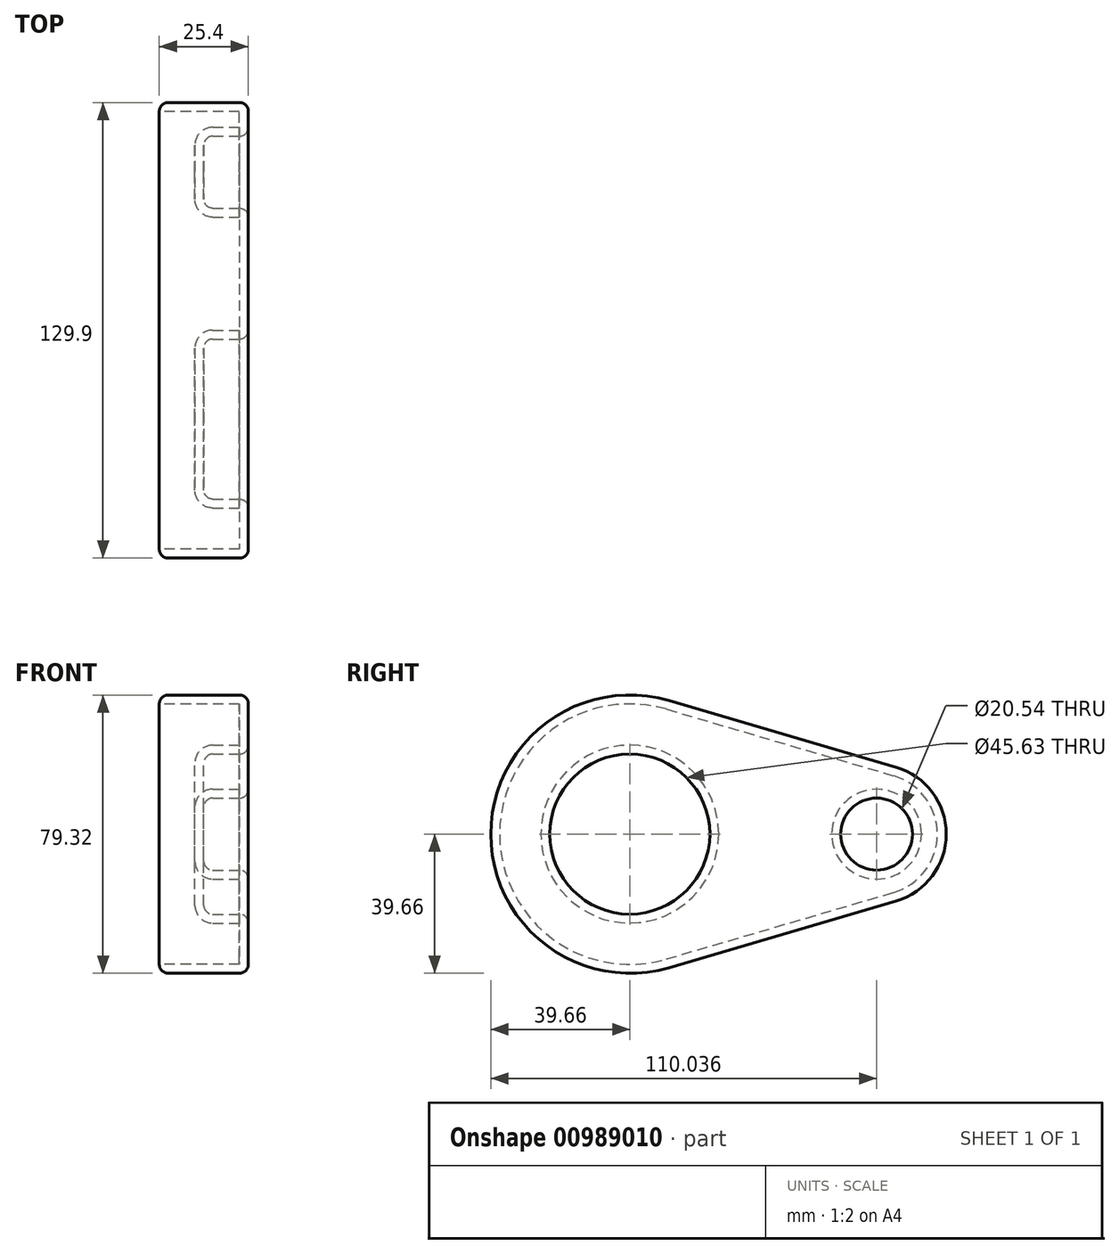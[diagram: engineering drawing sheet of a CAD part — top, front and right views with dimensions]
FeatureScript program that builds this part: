
annotation { "Feature Type Name" : "Feature", "Feature Type Description" : "" }
export const myFeature = defineFeature(function(context is Context, id is Id, definition is map)
    precondition{}
    {
        {
            var Q0;
            Q0=qCreatedBy(makeId("Right.planeOp"),FACE);
            var sketch = newSketch(context, id + "F0", { "sketchPlane" : qUnion([Q0])});
            skArc(sketch, "E0", {"start": v(11.15, 38.06) * mm, "mid": v(-39.66, 0) * mm, "end": v(11.15, -38.06) * mm});
            skArc(sketch, "E1", {"start": v(75.96, -19.06) * mm, "mid": v(90.24, 0) * mm, "end": v(75.96, 19.06) * mm});
            skLineSegment(sketch, "E2", {"start": v(11.15, 38.06) * mm, "end": v(75.96, 19.06) * mm});
            skLineSegment(sketch, "E3", {"start": v(11.15, -38.06) * mm, "end": v(75.96, -19.06) * mm});
            skSolve(sketch);
        }
        {
            var Q0;
            Q0=qSketchRegion(id+"F0",true);
            extrude(context, id + "F1", {"entities" : qUnion([Q0]), "depth" : 25.4 * mm});
        }
        {
            var Q0;
            Q0=makeQuery(id+"F1.opExtrude","CAP_FACE",FACE,{"disambiguationData":[OSD([sQuery(id+"F0.wireOp",EDGE,"E0"),sQuery(id+"F0.wireOp",EDGE,"E1"),sQuery(id+"F0.wireOp",EDGE,"E2"),sQuery(id+"F0.wireOp",EDGE,"E3")])],"isStart":false});
            var sketch = newSketch(context, id + "F2", { "sketchPlane" : qUnion([Q0])});
            skCircle(sketch, "E4", {"center": v(0, 0) * mm, "radius": 22.81 * mm});
            skCircle(sketch, "E5", {"center": v(70.38, 0) * mm, "radius": 10.27 * mm});
            skSolve(sketch);
        }
        {
            var Q0;
            Q0=qSketchRegion(id+"F2",true);
            extrude(context, id + "F3", {"entities" : qUnion([Q0]), "operationType" : NewBodyOperationType.REMOVE, "oppositeDirection" : true, "depth" : 12.7 * mm});
        }
        {
            var Q0;
            Q0=makeQuery(id+"F1.opExtrude","CAP_FACE",FACE,{"disambiguationData":[OSD([sQuery(id+"F0.wireOp",EDGE,"E0"),sQuery(id+"F0.wireOp",EDGE,"E1"),sQuery(id+"F0.wireOp",EDGE,"E2"),sQuery(id+"F0.wireOp",EDGE,"E3")])],"isStart":false});
            var Q1;
            Q1=makeQuery(id+"F3.boolean.opBoolean","COPY",FACE,{"derivedFrom":makeQuery(id+"F3.opExtrude","CAP_FACE",FACE,{"disambiguationData":[OSD([sQuery(id+"F2.wireOp",EDGE,"E4")])],"isStart":false})});
            var Q2;
            Q2=makeQuery(id+"F3.boolean.opBoolean","COPY",FACE,{"derivedFrom":makeQuery(id+"F3.opExtrude","CAP_FACE",FACE,{"disambiguationData":[OSD([sQuery(id+"F2.wireOp",EDGE,"E5")])],"isStart":false})});
            var Q3;
            Q3=makeQuery(id+"F1.opExtrude","CAP_FACE",FACE,{"disambiguationData":[OSD([sQuery(id+"F0.wireOp",EDGE,"E0"),sQuery(id+"F0.wireOp",EDGE,"E1"),sQuery(id+"F0.wireOp",EDGE,"E2"),sQuery(id+"F0.wireOp",EDGE,"E3")])],"isStart":true});
            fillet(context, id + "F4", {"entities" : qUnion([Q0, Q1, Q2, Q3]), "radius" : 2.54 * mm, "tangentPropagation" : true, "allowEdgeOverflow" : false});
        }
        {
            var Q0;
            Q0=makeQuery(id+"F1.opExtrude","CAP_FACE",FACE,{"disambiguationData":[OSD([sQuery(id+"F0.wireOp",EDGE,"E0"),sQuery(id+"F0.wireOp",EDGE,"E1"),sQuery(id+"F0.wireOp",EDGE,"E2"),sQuery(id+"F0.wireOp",EDGE,"E3")])],"isStart":true});
            shell(context, id + "F5", {"entities" : qUnion([Q0]), "thickness" : 2.54 * mm});
        }
    });
